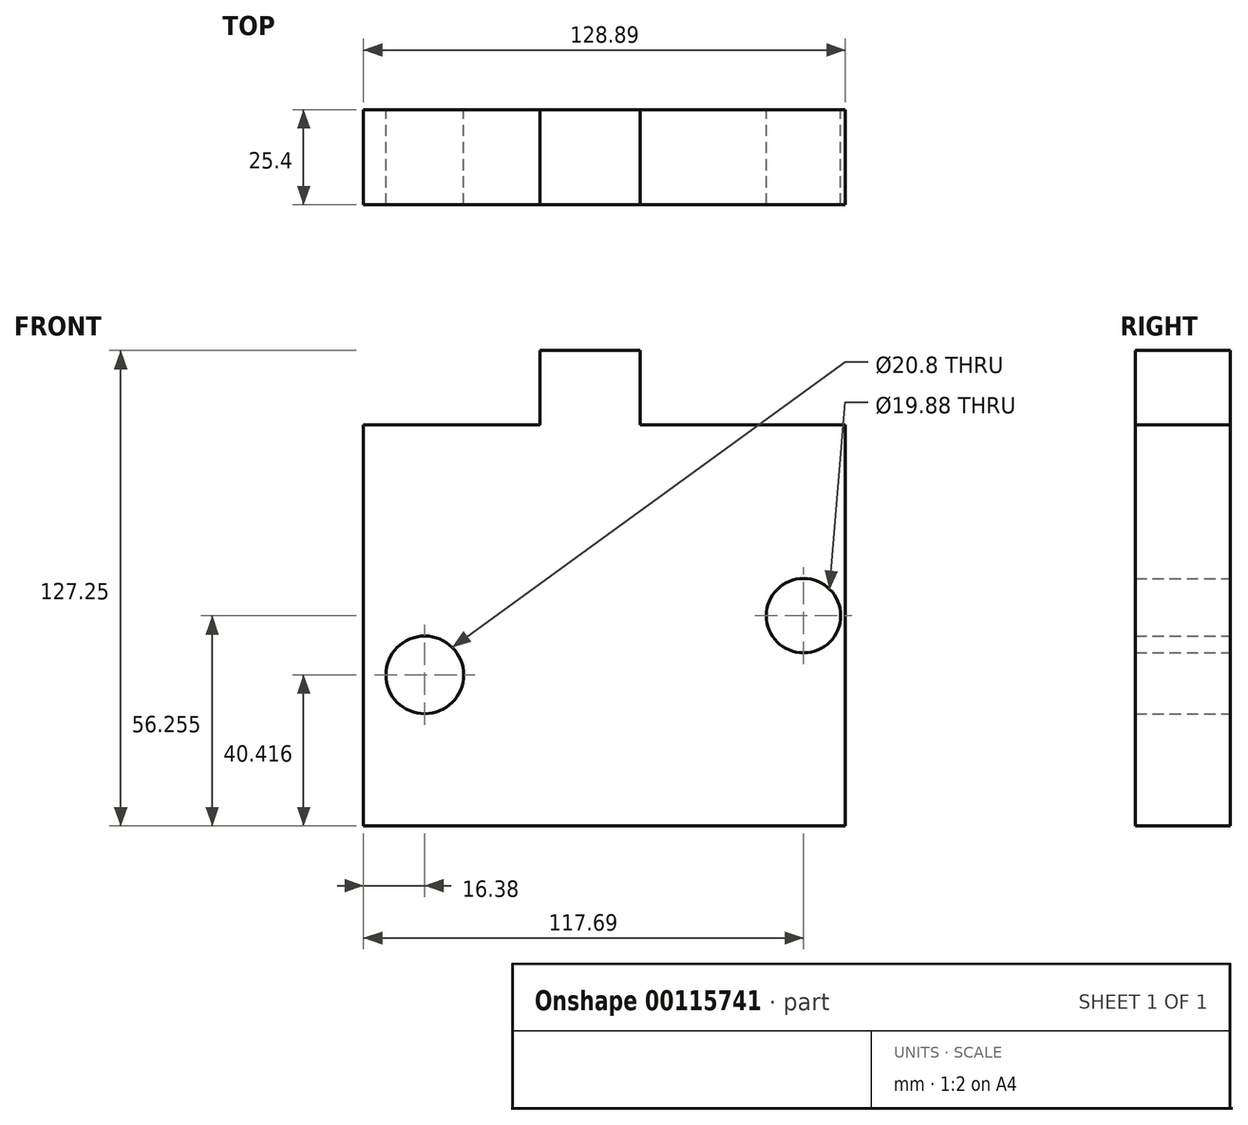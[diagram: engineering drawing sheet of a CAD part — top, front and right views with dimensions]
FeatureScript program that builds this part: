
annotation { "Feature Type Name" : "Feature", "Feature Type Description" : "" }
export const myFeature = defineFeature(function(context is Context, id is Id, definition is map)
    precondition{}
    {
        {
            var Q0;
            Q0=qCreatedBy(makeId("Front.planeOp"),FACE);
            var sketch = newSketch(context, id + "F0", { "sketchPlane" : qUnion([Q0])});
            skLineSegment(sketch, "E0.bottom", {"start": v(-58.16, -54.07) * mm, "end": v(70.73, -54.07) * mm});
            skLineSegment(sketch, "E0.top", {"start": v(-58.16, 53.25) * mm, "end": v(70.73, 53.25) * mm});
            skLineSegment(sketch, "E0.left", {"start": v(-58.16, -54.07) * mm, "end": v(-58.16, 53.25) * mm});
            skLineSegment(sketch, "E0.right", {"start": v(70.73, -54.07) * mm, "end": v(70.73, 53.25) * mm});
            skLineSegment(sketch, "E1", {"start": v(-10.92, 53.25) * mm, "end": v(-10.92, 73.18) * mm});
            skLineSegment(sketch, "E2", {"start": v(-10.92, 73.18) * mm, "end": v(15.84, 73.18) * mm});
            skLineSegment(sketch, "E3", {"start": v(15.84, 73.18) * mm, "end": v(15.84, 53.25) * mm});
            skCircle(sketch, "E4", {"center": v(-41.78, -13.65) * mm, "radius": 10.4 * mm});
            skCircle(sketch, "E5", {"center": v(59.53, 2.18) * mm, "radius": 9.94 * mm});
            skSolve(sketch);
        }
        {
            var Q0;
            {var subQ0=sQuery(id+"F0.wireOp",EDGE,"E1");Q0=makeQuery(id+"F0.imprint","IMPRINT",FACE,{"disambiguationData":[TD([[makeQuery(id+"F0.imprint","IMPRINT",EDGE,{"derivedFrom":subQ0}),-1.0]])]});}
            var Q1;
            Q1=makeQuery(id+"F0.imprint","IMPRINT",FACE,{"disambiguationData":[TD([[makeQuery(id+"F0.imprint","IMPRINT",EDGE,{"derivedFrom":sQuery(id+"F0.wireOp",EDGE,"E0.bottom")}),1.0]])]});
            extrude(context, id + "F1", {"entities" : qUnion([Q0, Q1]), "depth" : 25.4 * mm});
        }
    });
